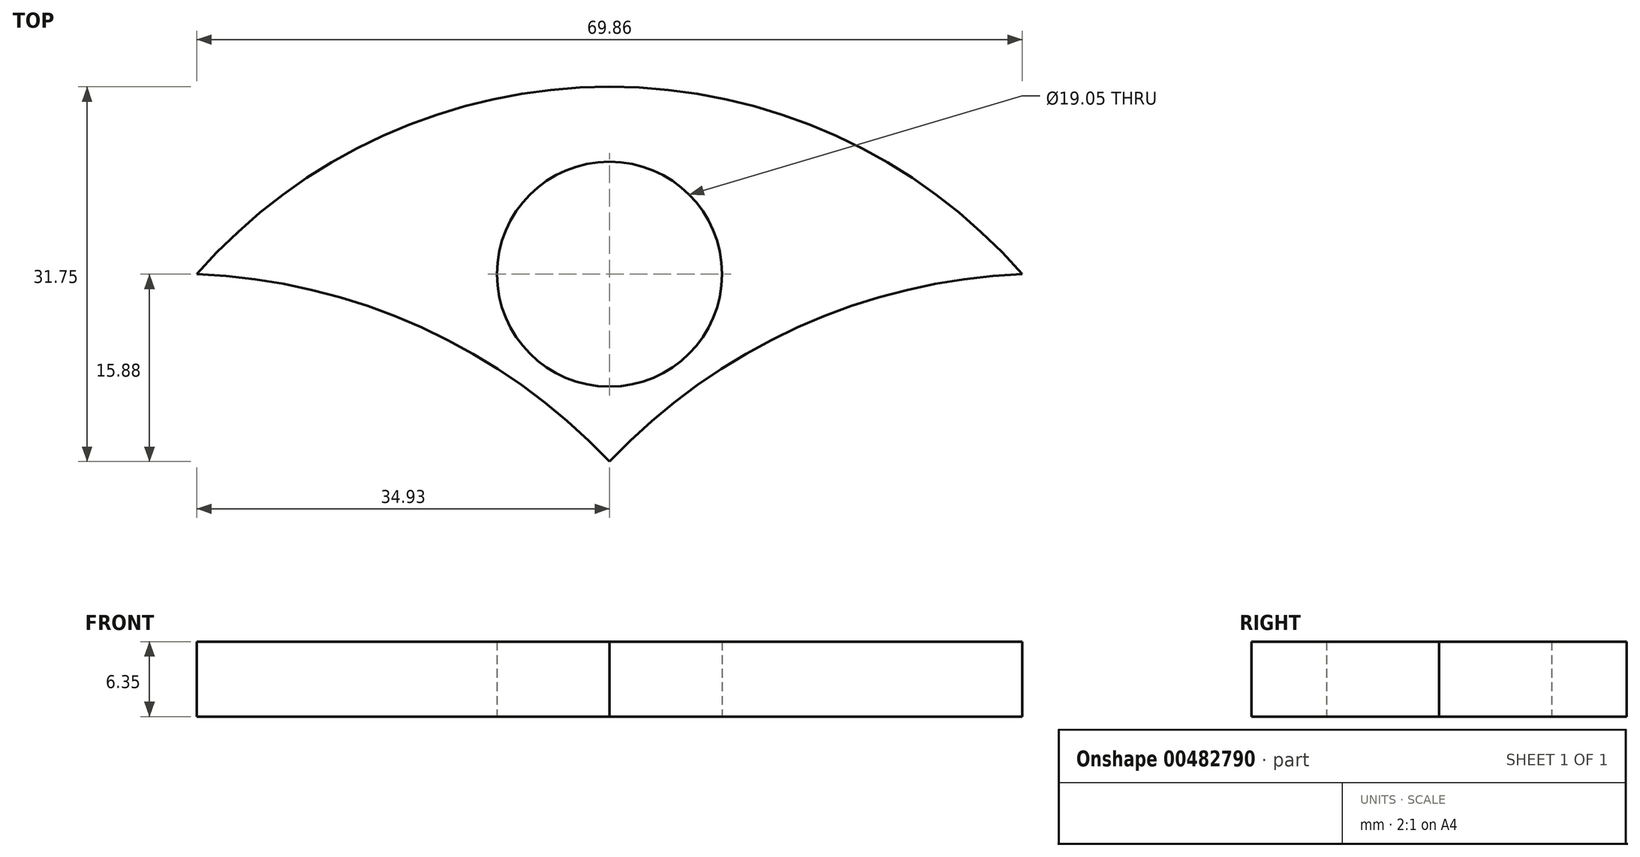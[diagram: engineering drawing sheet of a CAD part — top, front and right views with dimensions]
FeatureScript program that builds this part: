
annotation { "Feature Type Name" : "Feature", "Feature Type Description" : "" }
export const myFeature = defineFeature(function(context is Context, id is Id, definition is map)
    precondition{}
    {
        {
            var Q0;
            Q0=qCreatedBy(makeId("Top.planeOp"),FACE);
            var sketch = newSketch(context, id + "F0", { "sketchPlane" : qUnion([Q0])});
            skCircle(sketch, "E0", {"center": v(0, 0) * mm, "radius": 9.53 * mm});
            skArc(sketch, "E1", {"start": v(34.92, 0) * mm, "mid": v(0, 15.87) * mm, "end": v(-34.93, 0) * mm});
            skArc(sketch, "E2", {"start": v(34.93, 0) * mm, "mid": v(15.9, -4.51) * mm, "end": v(0, -15.88) * mm});
            skArc(sketch, "E3.MirrorCS", {"start": v(-34.93, 0) * mm, "mid": v(-15.9, -4.51) * mm, "end": v(0, -15.88) * mm});
            skSolve(sketch);
        }
        {
            var Q0;
            Q0=makeQuery(id+"F0.imprint","IMPRINT",FACE,{"disambiguationData":[TD([[makeQuery(id+"F0.imprint","IMPRINT",EDGE,{"derivedFrom":sQuery(id+"F0.wireOp",EDGE,"E0")}),-1.0]])]});
            extrude(context, id + "F1", {"entities" : qUnion([Q0]), "depth" : 6.35 * mm});
        }
    });
